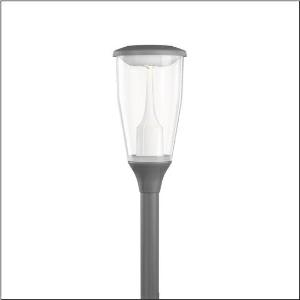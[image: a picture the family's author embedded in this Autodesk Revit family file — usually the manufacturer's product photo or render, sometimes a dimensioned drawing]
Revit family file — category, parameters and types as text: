
# Revit family: dl_11_iq___st1_2a_5xa5575mf14h000022_93a8
name_source: partatom
category: Lighting Fixtures
units: mm (PartAtom-declared; Revit-internal decimal feet)

## family parameters
Cut with Voids When Loaded = No
Host = Face
Light Source = No
Part Type = Normal
Room Calculation Point = No
Round Connector Dimension = Use Diameter
Shared = No

## types (1)
- --- (1 x LED, 1560 lm, 11.8 W, 2700K)
    Apparent Load = 12 VA
    CIE Flux Codes = 24 63 94 96 100
    Color Rendering = 70
    Color Temperature = 2700K
    Default Elevation = 1800 mm
    Description = DL 11 iQ, mast luminaire, Module 540 iQ-SR, primary light control with 3 zone facetted reflector, of plastic, silver coated, highly specular, structured, primary optical cover: cover, of PMMA, transparent, light distribution: ST1.2a, light emission: direct distribution, primary light characteristic: asymmetric, installation type: post-top, LED, High Power LED, rated luminous flux: 1.560lm, luminous efficacy: 149lm/W, light colour: 727, colour temperature: 2700K, control: Street-Remote, Auto-Match, Temp-Guard, Lumen-Switch, Night-Set, Smart-Wire, Light-Fading, Desk-Remote (wireless, voltage-free reading and setting of iQ features in the workshop via application-optimized NFC function/RFID function), optimised constant luminous flux control (CLO 2.0), mains connection: 220..240V, AC, 50/60Hz, connection cable pre-assembled, cable length: 5,5m, wiring characteristics: H07RN-F, 5-core, 1.5mm², start of lifetime: 12W, end of service life: 12W, reduction: 5W, luminaire housing, upper part, of diecast aluminium, coated, Siteco® metallic grey (DB 702S), spigot size: 76mm (post-top), post-top mast mounting element, of diecast aluminium, coated, Siteco® metallic grey (DB 702S), Module 540 iQ-SR, traffic white (RAL 9016), equipment: standard, protection rating (complete): IP66, insulation class (complete): insulation class II (safety insulation), certification: CE, ENEC, ENEC+, VDE, packaging unit: 1 piece

Light Distribution: ST1.2a
    Height = 665 mm
    Lamp = 1 x LED
    Lamp Light Flux = 1560 lm
    Lamp Power = 11.8 W
    Lamp count = 1
    Length = 334 mm
    Luminous efficacy = 132 lm/W
    Manufacturer = Siteco
    ModVariant = No
    Model = 5XA5575MF14H000022
    Number of Poles = 1
    OnlyDefault = Yes
    Power Factor = 1
    Product Name = DL 11 iQ | ST1.2a
    Product group = mast luminaire | pylon top
    ProductGroupID = 6100
    Protection Class = Protection class II
    Protection Degree = IP 66
    RLX_Detail_Level = 1
    RLX_Emergency_Light_Flux = 0 lm
    RLX_Emergency_Type = 0
    RLX_Emergency_Type_DB = No
    RlxData = <blob elided: 153477 chars, md5=14b06424>
    Socket = socket
    Standby Power = 0 W
    System Light Flux = 1560 lm
    System Power = 12 W
    Type Comments = factory setting: luminous flux: 100 % | dim-lin: 254 | 472 mA
    Type Image = l_1258354.jpg
    URL = http://relux.com
    VarID = @adj_063679
    Voltage = 0 V
    Weight = 0.00 kg
    Width = 0 mm  [stored 0 ft]

note: [stored X ft] marks values corroborated as IEEE doubles in the binary element streams (Revit-internal decimal feet)

## geometry (parser evidence)
native form markers: Blend x4, Sweep x9
no freeform markers — native parametric forms only
